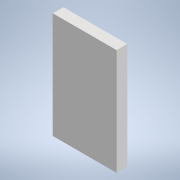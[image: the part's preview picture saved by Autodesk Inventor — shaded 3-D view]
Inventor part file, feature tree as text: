
AUTODESK INVENTOR PART (.ipt)
format: ipt  version: 2022 (Build 260153000, 153)  size: 91,136 bytes
history: native  units: mm
features: other x1, extrude x1, sketch x1
ambient origin geometry x8: Origin, YZ Plane, XZ Plane, XY Plane, X Axis, Y Axis, Z Axis, Center Point
bodies: Body1 (feature_tree)
feature tree (3):
  other  "ソリッド1"
  extrude  "押し出し1"  Depth=5.0mm
  sketch  "スケッチ1"
